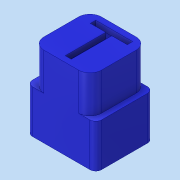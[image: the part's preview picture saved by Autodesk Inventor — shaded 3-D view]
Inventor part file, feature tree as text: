
AUTODESK INVENTOR PART (.ipt)
format: ipt  version: 2018 (Build 220112000, 112)  size: 164,352 bytes
history: native  units: mm
features: sketch x3, extrude x2, fillet x2, other x1, projected_geometry x1
ambient origin geometry x8: Origin, YZ Plane, XZ Plane, XY Plane, X Axis, Y Axis, Z Axis, Center Point
bodies: Volumenkörper1 (feature_tree)
feature tree (9):
  extrude  "Extrusion1"  Depth=10.0mm
  extrude  "Extrusion2"  Depth=10.0mm
  fillet  "Rundung1"  Radius=10.0mm
  fillet  "Rundung2"  Radius=6.5mm
  other  "Prägen1"
  sketch  "Skizze1"  dims[d0=12.0mm d1=10.0mm]
  sketch  "Skizze2"  dims[d2=14.0mm d3=0.0mm d4=10.0mm d5=10.0mm d6=6.5mm d7=0.0mm]
  sketch  "Skizze3"  dims[d8=2.0mm d9=1.0mm d10=1.0mm d11=1.0mm d12=1.0mm d13=3.490659mm]
  projected_geometry  "Projizierte Kontur1"
